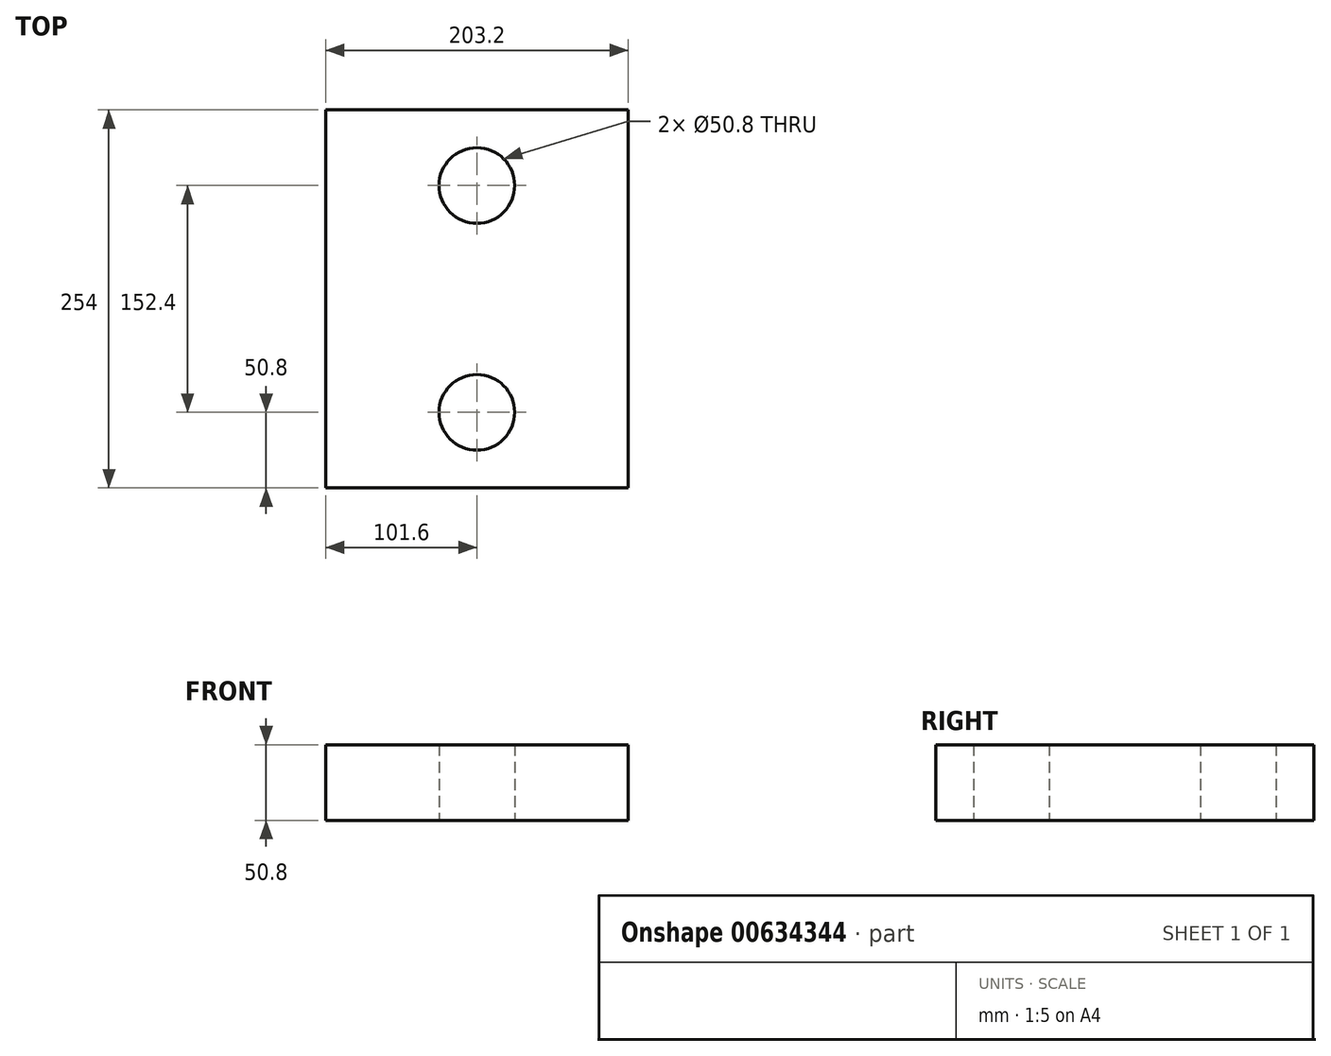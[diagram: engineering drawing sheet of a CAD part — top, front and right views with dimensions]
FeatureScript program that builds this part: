
annotation { "Feature Type Name" : "Feature", "Feature Type Description" : "" }
export const myFeature = defineFeature(function(context is Context, id is Id, definition is map)
    precondition{}
    {
        {
            var Q0;
            Q0=qCreatedBy(makeId("Top.planeOp"),FACE);
            var sketch = newSketch(context, id + "F0", { "sketchPlane" : qUnion([Q0])});
            skLineSegment(sketch, "E0.bottom", {"start": v(0, 0) * mm, "end": v(203.2, 0) * mm});
            skLineSegment(sketch, "E0.top", {"start": v(0, 254) * mm, "end": v(203.2, 254) * mm});
            skLineSegment(sketch, "E0.left", {"start": v(0, 0) * mm, "end": v(0, 254) * mm});
            skLineSegment(sketch, "E0.right", {"start": v(203.2, 0) * mm, "end": v(203.2, 254) * mm});
            skCircle(sketch, "E1", {"center": v(101.6, 203.2) * mm, "radius": 25.4 * mm});
            skPoint(sketch, "E1.centerSnap0", {"position": v(101.6, 0) * mm});
            skLineSegment(sketch, "E2", {"start": v(0, 127) * mm, "end": v(203.2, 127) * mm, "construction": true});
            skCircle(sketch, "E3.MirrorC", {"center": v(101.6, 50.8) * mm, "radius": 25.4 * mm});
            skSolve(sketch);
        }
        {
            var Q0;
            Q0=makeQuery(id+"F0.imprint","IMPRINT",FACE,{"disambiguationData":[TD([[makeQuery(id+"F0.imprint","IMPRINT",EDGE,{"derivedFrom":sQuery(id+"F0.wireOp",EDGE,"E0.bottom")}),1.0]])]});
            extrude(context, id + "F1", {"entities" : qUnion([Q0]), "depth" : 50.8 * mm, "offsetDistance" : 25.4 * mm});
        }
    });
